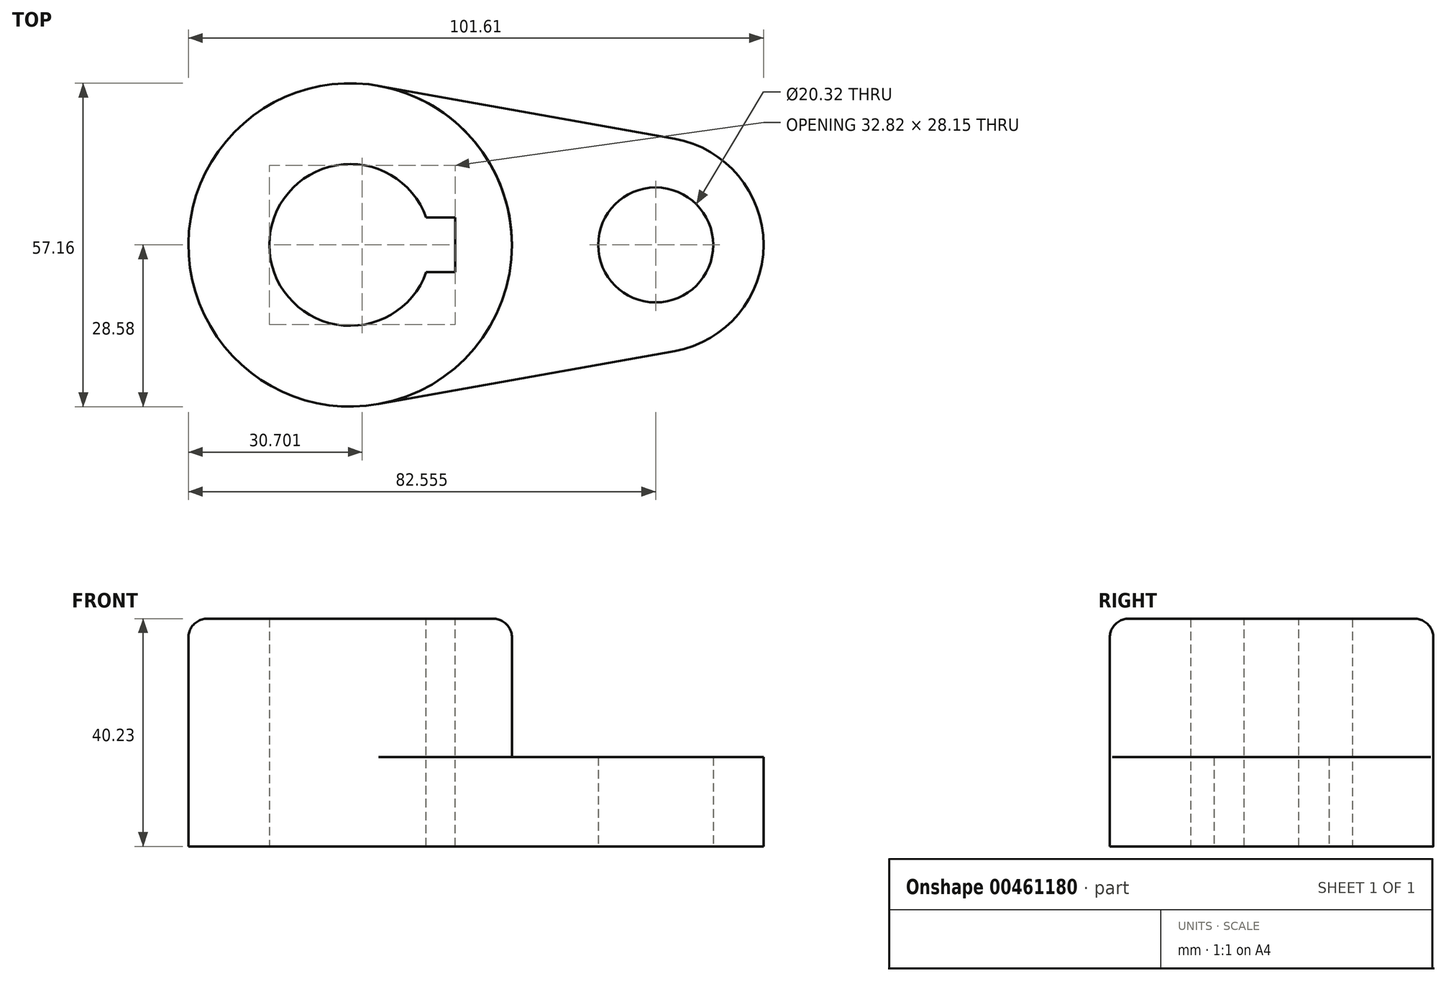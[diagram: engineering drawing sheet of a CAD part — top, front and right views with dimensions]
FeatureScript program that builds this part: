
annotation { "Feature Type Name" : "Feature", "Feature Type Description" : "" }
export const myFeature = defineFeature(function(context is Context, id is Id, definition is map)
    precondition{}
    {
        {
            var Q0;
            Q0=qCreatedBy(makeId("Top.planeOp"),FACE);
            var sketch = newSketch(context, id + "F0", { "sketchPlane" : qUnion([Q0])});
            skCircle(sketch, "E0", {"center": v(0, 0) * mm, "radius": 14.29 * mm});
            skCircle(sketch, "E1", {"center": v(0, 0) * mm, "radius": 28.58 * mm});
            skCircle(sketch, "E2", {"center": v(53.98, 0) * mm, "radius": 10.16 * mm});
            skCircle(sketch, "E3", {"center": v(53.98, 0) * mm, "radius": 19.05 * mm});
            skLineSegment(sketch, "E4", {"start": v(57.34, 18.75) * mm, "end": v(5.04, 28.13) * mm});
            skLineSegment(sketch, "E5", {"start": v(5.04, -28.13) * mm, "end": v(57.34, -18.75) * mm});
            skSolve(sketch);
        }
        {
            var Q0;
            Q0 = qSketchRegion(id + "F0", true);
            extrude(context, id + "F1", {"entities" : qUnion([Q0]), "depth" : 15.77 * mm});
        }
        {
            var Q0;
            Q0=makeQuery(id+"F1.opExtrude","CAP_FACE",FACE,{"disambiguationData":[OSD([sQuery(id+"F0.wireOp",EDGE,"E0"),sQuery(id+"F0.wireOp",EDGE,"E1"),sQuery(id+"F0.wireOp",EDGE,"E2"),sQuery(id+"F0.wireOp",EDGE,"E3"),sQuery(id+"F0.wireOp",EDGE,"E4"),sQuery(id+"F0.wireOp",EDGE,"E5")])],"isStart":false});
            var sketch = newSketch(context, id + "F2", { "sketchPlane" : qUnion([Q0])});
            skCircle(sketch, "E6.0", {"center": v(0, 0) * mm, "radius": 28.58 * mm});
            skCircle(sketch, "E7.0", {"center": v(0, 0) * mm, "radius": 14.29 * mm});
            skSolve(sketch);
        }
        {
            var Q0;
            Q0 = qSketchRegion(id + "F2", true);
            extrude(context, id + "F3", {"entities" : qUnion([Q0]), "operationType" : NewBodyOperationType.ADD, "depth" : 24.46 * mm});
        }
        {
            var Q0;
            Q0=makeQuery(id+"F3.opExtrude","CAP_FACE",FACE,{"disambiguationData":[OSD([sQuery(id+"F2.wireOp",EDGE,"E6.0"),sQuery(id+"F2.wireOp",EDGE,"E7.0")])],"isStart":false});
            var sketch = newSketch(context, id + "F4", { "sketchPlane" : qUnion([Q0])});
            skLineSegment(sketch, "E8.bottom", {"start": v(18.53, 4.83) * mm, "end": v(-14.29, 4.83) * mm});
            skLineSegment(sketch, "E8.top", {"start": v(18.53, -4.83) * mm, "end": v(-14.29, -4.83) * mm});
            skLineSegment(sketch, "E8.left", {"start": v(18.53, 4.83) * mm, "end": v(18.53, -4.83) * mm});
            skLineSegment(sketch, "E8.right", {"start": v(-14.29, 4.83) * mm, "end": v(-14.29, -4.83) * mm});
            skPoint(sketch, "E8.middle", {"position": v(2.12, 0) * mm});
            skSolve(sketch);
        }
        {
            var Q0;
            {var subQ0=sQuery(id+"F4.wireOp",EDGE,"E8.left");Q0=makeQuery(id+"F4.imprint","IMPRINT",FACE,{"disambiguationData":[TD([[makeQuery(id+"F4.imprint","IMPRINT",EDGE,{"derivedFrom":subQ0}),-1.0]])]});}
            var Q1;
            Q1=makeQuery(id+"F1.opExtrude","CAP_FACE",FACE,{"disambiguationData":[OSD([sQuery(id+"F0.wireOp",EDGE,"E0"),sQuery(id+"F0.wireOp",EDGE,"E1"),sQuery(id+"F0.wireOp",EDGE,"E2"),sQuery(id+"F0.wireOp",EDGE,"E3"),sQuery(id+"F0.wireOp",EDGE,"E4"),sQuery(id+"F0.wireOp",EDGE,"E5")])],"isStart":true});
            extrude(context, id + "F5", {"entities" : qUnion([Q0]), "operationType" : NewBodyOperationType.REMOVE, "endBound" : BoundingType.UP_TO_SURFACE, "oppositeDirection" : true, "endBoundEntityFace" : qUnion([Q1]), "depth" : 25.4 * mm});
        }
        {
            var Q0;
            Q0=makeQuery(id+"F3.opExtrude","CAP_EDGE",EDGE,{"disambiguationData":[OSD([sQuery(id+"F2.wireOp",EDGE,"E6.0")])],"isStart":false});
            fillet(context, id + "F6", {"entities" : qUnion([Q0]), "radius" : 3.3 * mm, "tangentPropagation" : true, "allowEdgeOverflow" : false});
        }
    });
